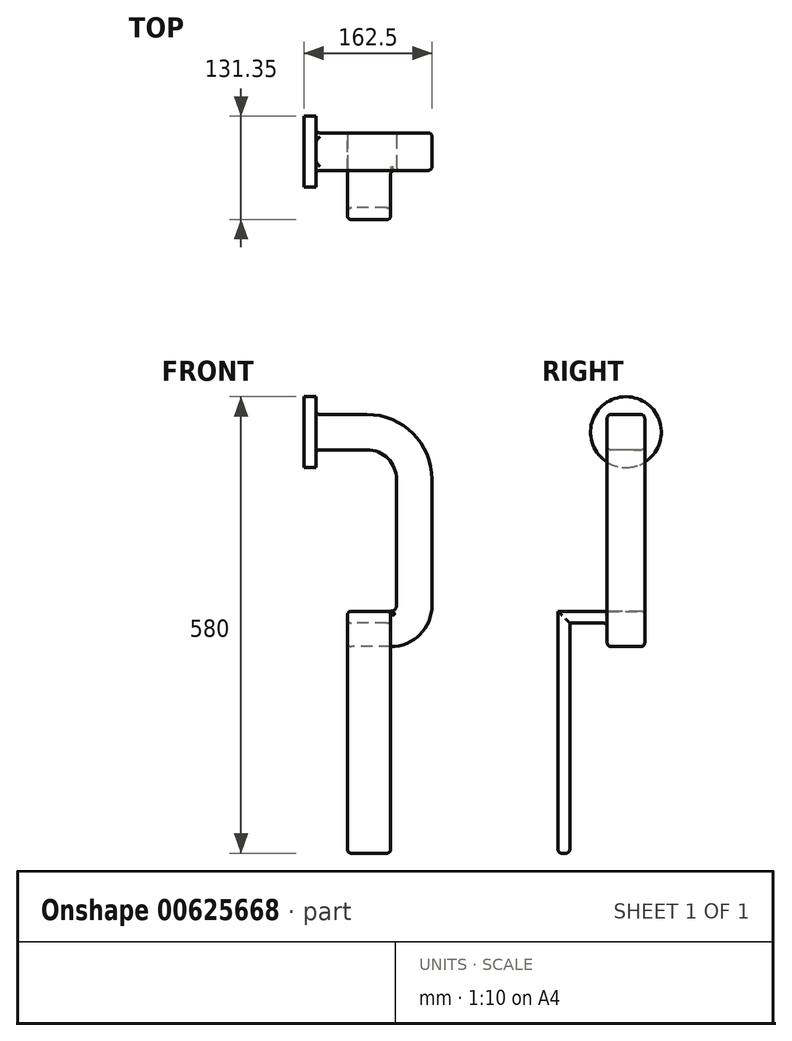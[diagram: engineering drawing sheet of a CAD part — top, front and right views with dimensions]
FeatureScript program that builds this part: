
annotation { "Feature Type Name" : "Feature", "Feature Type Description" : "" }
export const myFeature = defineFeature(function(context is Context, id is Id, definition is map)
    precondition{}
    {
        {
            var Q0;
            Q0=qCreatedBy(makeId("Right.planeOp"),FACE);
            var sketch = newSketch(context, id + "F0", { "sketchPlane" : qUnion([Q0])});
            skCircle(sketch, "E0", {"center": v(0, 0) * mm, "radius": 45 * mm});
            skSolve(sketch);
        }
        {
            var Q0;
            Q0=makeQuery(id+"F0.imprint","IMPRINT",FACE,{"disambiguationData":[TD([[makeQuery(id+"F0.imprint","IMPRINT",EDGE,{"derivedFrom":sQuery(id+"F0.wireOp",EDGE,"E0")}),1.0]])]});
            var Q1;
            Q1=sQuery(id+"F0.wireOp",EDGE,"E0");
            extrude(context, id + "F1", {"entities" : qUnion([Q0]), "surfaceEntities" : qUnion([Q1]), "depth" : 15 * mm, "offsetDistance" : 25 * mm});
        }
        {
            var Q0;
            Q0=makeQuery(id+"F1.opExtrude","CAP_FACE",FACE,{"disambiguationData":[OSD([sQuery(id+"F0.wireOp",EDGE,"E0")])],"isStart":false});
            var sketch = newSketch(context, id + "F2", { "sketchPlane" : qUnion([Q0])});
            skLineSegment(sketch, "E1.bottom", {"start": v(23.85, -22.5) * mm, "end": v(-23.85, -22.5) * mm});
            skLineSegment(sketch, "E1.top", {"start": v(23.85, 22.5) * mm, "end": v(-23.85, 22.5) * mm});
            skLineSegment(sketch, "E1.left", {"start": v(23.85, -22.5) * mm, "end": v(23.85, 22.5) * mm});
            skLineSegment(sketch, "E1.right", {"start": v(-23.85, -22.5) * mm, "end": v(-23.85, 22.5) * mm});
            skPoint(sketch, "E1.middle", {"position": v(0, 0) * mm});
            skSolve(sketch);
        }
        {
            var Q0;
            Q0=qCreatedBy(makeId("Front.planeOp"),FACE);
            var sketch = newSketch(context, id + "F3", { "sketchPlane" : qUnion([Q0])});
            skLineSegment(sketch, "E2", {"start": v(15, 0) * mm, "end": v(80, 0) * mm});
            skLineSegment(sketch, "E3", {"start": v(140, -60) * mm, "end": v(140, -220) * mm});
            skLineSegment(sketch, "E4", {"start": v(110, -250) * mm, "end": v(55, -250) * mm});
            skPoint(sketch, "E5.visualSharp", {"position": v(140, 0) * mm});
            skArc(sketch, "E5.filletArc", {"start": v(140, -60) * mm, "mid": v(122.43, -17.57) * mm, "end": v(80, 0) * mm});
            skPoint(sketch, "E6.visualSharp", {"position": v(140, -250) * mm});
            skArc(sketch, "E6.filletArc", {"start": v(110, -250) * mm, "mid": v(131.21, -241.21) * mm, "end": v(140, -220) * mm});
            skSolve(sketch);
        }
        {
            var Q0;
            Q0=makeQuery(id+"F2.imprint","IMPRINT",FACE,{"disambiguationData":[TD([[makeQuery(id+"F2.imprint","IMPRINT",EDGE,{"derivedFrom":sQuery(id+"F2.wireOp",EDGE,"E1.bottom")}),-1.0]])]});
            var Q1;
            Q1=sQuery(id+"F3.wireOp",EDGE,"E2");
            var Q2;
            Q2=sQuery(id+"F3.wireOp",EDGE,"E5.filletArc");
            var Q3;
            Q3=sQuery(id+"F3.wireOp",EDGE,"E3");
            var Q4;
            Q4=sQuery(id+"F3.wireOp",EDGE,"E6.filletArc");
            var Q5;
            Q5=sQuery(id+"F3.wireOp",EDGE,"E4");
            var Q6;
            Q6=sQuery(id+"F3.wireOp",EDGE,"f7d318e7-d869-4865-ad89-960b62a924f9.filletArc");
            var Q7;
            Q7=sQuery(id+"F3.wireOp",EDGE,"3ABNLYvD-kYsS-FpID-JL3W-QJcLAkyu1SoM");
            sweep(context, id + "F4", {"operationType" : NewBodyOperationType.ADD, "profiles" : qUnion([Q0]), "path" : qUnion([Q1, Q2, Q3, Q4, Q5, Q6, Q7])});
        }
        {
            var Q0;
            Q0=makeQuery(id+"F4.opSweep","SWEPT_FACE",FACE,{"disambiguationData":[OSD([sQuery(id+"F2.wireOp",EDGE,"E1.right"),sQuery(id+"F3.wireOp",EDGE,"E2")])]});
            var sketch = newSketch(context, id + "F5", { "sketchPlane" : qUnion([Q0])});
            skLineSegment(sketch, "E7.bottom", {"start": v(55, -227.5) * mm, "end": v(110, -227.5) * mm});
            skLineSegment(sketch, "E7.top", {"start": v(55, -242.5) * mm, "end": v(110, -242.5) * mm});
            skLineSegment(sketch, "E7.left", {"start": v(55, -227.5) * mm, "end": v(55, -242.5) * mm});
            skLineSegment(sketch, "E7.right", {"start": v(110, -227.5) * mm, "end": v(110, -242.5) * mm});
            skSolve(sketch);
        }
        {
            var Q0;
            Q0=sQuery(id+"F5.wireOp",EDGE,"E7.left");
            cPoint(context, id + "F6", {"entities" : qUnion([Q0]), "parameter" : 0.5});
        }
        {
            var Q0;
            Q0=sQuery(id+"F5.wireOp",EDGE,"E7.right");
            cPoint(context, id + "F7", {"entities" : qUnion([Q0]), "parameter" : 0.5});
        }
        {
            var Q0;
            Q0 = qCreatedBy(id + "F6" ,VERTEX);
            var Q1;
            Q1 = qCreatedBy(id + "F7" ,VERTEX);
            cPlane(context, id + "F8", {"entities" : qUnion([Q0, Q1]), "cplaneType" : CPlaneType.MID_PLANE, "offset" : 25 * mm, "width" : 150 * mm, "height" : 150 * mm});
        }
        {
            var Q0;
            Q0=qCreatedBy(id+"F8.planeOp",FACE);
            var sketch = newSketch(context, id + "F9", { "sketchPlane" : qUnion([Q0])});
            skLineSegment(sketch, "E8", {"start": v(-23.85, -235) * mm, "end": v(-78.85, -235) * mm});
            skLineSegment(sketch, "E9", {"start": v(-78.85, -235) * mm, "end": v(-78.85, -535) * mm});
            skSolve(sketch);
        }
        {
            var Q0;
            Q0=makeQuery(id+"F5.imprint","IMPRINT",FACE,{"disambiguationData":[TD([[makeQuery(id+"F5.imprint","IMPRINT",EDGE,{"derivedFrom":sQuery(id+"F5.wireOp",EDGE,"E7.bottom")}),1.0]])]});
            var Q1;
            Q1=sQuery(id+"F9.wireOp",EDGE,"E8");
            var Q2;
            Q2=sQuery(id+"F9.wireOp",EDGE,"E9");
            sweep(context, id + "F10", {"operationType" : NewBodyOperationType.ADD, "profiles" : qUnion([Q0]), "path" : qUnion([Q1, Q2])});
        }
        {
            var Q0;
            Q0=makeQuery(id+"F4.opSweep","SWEPT_FACE",FACE,{"disambiguationData":[OSD([sQuery(id+"F2.wireOp",EDGE,"E1.right"),sQuery(id+"F3.wireOp",EDGE,"E2")])]});
            var Q1;
            Q1=makeQuery(id+"F10.opSweep","SWEPT_FACE",FACE,{"disambiguationData":[OSD([sQuery(id+"F5.wireOp",EDGE,"E7.right"),sQuery(id+"F9.wireOp",EDGE,"E8")])]});
            var Q2;
            Q2=makeQuery(id+"F4.opSweep","SWEPT_FACE",FACE,{"disambiguationData":[OSD([sQuery(id+"F2.wireOp",EDGE,"E1.left"),sQuery(id+"F3.wireOp",EDGE,"E2")])]});
            var Q3;
            Q3=makeQuery(id+"F10.boolean.opBoolean","MERGE",FACE,{"derivedFrom":[makeQuery(id+"F4.opSweep","CAP_FACE",FACE,{"disambiguationData":[OSD([sQuery(id+"F2.wireOp",EDGE,"E1.bottom"),sQuery(id+"F2.wireOp",EDGE,"E1.top"),sQuery(id+"F2.wireOp",EDGE,"E1.left"),sQuery(id+"F2.wireOp",EDGE,"E1.right"),sQuery(id+"F3.wireOp",VERTEX,"E4.end")])],"isStart":false}),makeQuery(id+"F10.opSweep","SWEPT_FACE",FACE,{"disambiguationData":[OSD([sQuery(id+"F5.wireOp",EDGE,"E7.left"),sQuery(id+"F9.wireOp",EDGE,"E8")])]})]});
            var Q4;
            Q4=makeQuery(id+"F10.opSweep","CAP_FACE",FACE,{"disambiguationData":[OSD([sQuery(id+"F5.wireOp",EDGE,"E7.bottom"),sQuery(id+"F5.wireOp",EDGE,"E7.top"),sQuery(id+"F5.wireOp",EDGE,"E7.left"),sQuery(id+"F5.wireOp",EDGE,"E7.right"),sQuery(id+"F9.wireOp",VERTEX,"E9.end")])],"isStart":false});
            fillet(context, id + "F11", {"entities" : qUnion([Q0, Q1, Q2, Q3, Q4]), "radius" : 5 * mm, "tangentPropagation" : true, "allowEdgeOverflow" : false});
        }
    });
